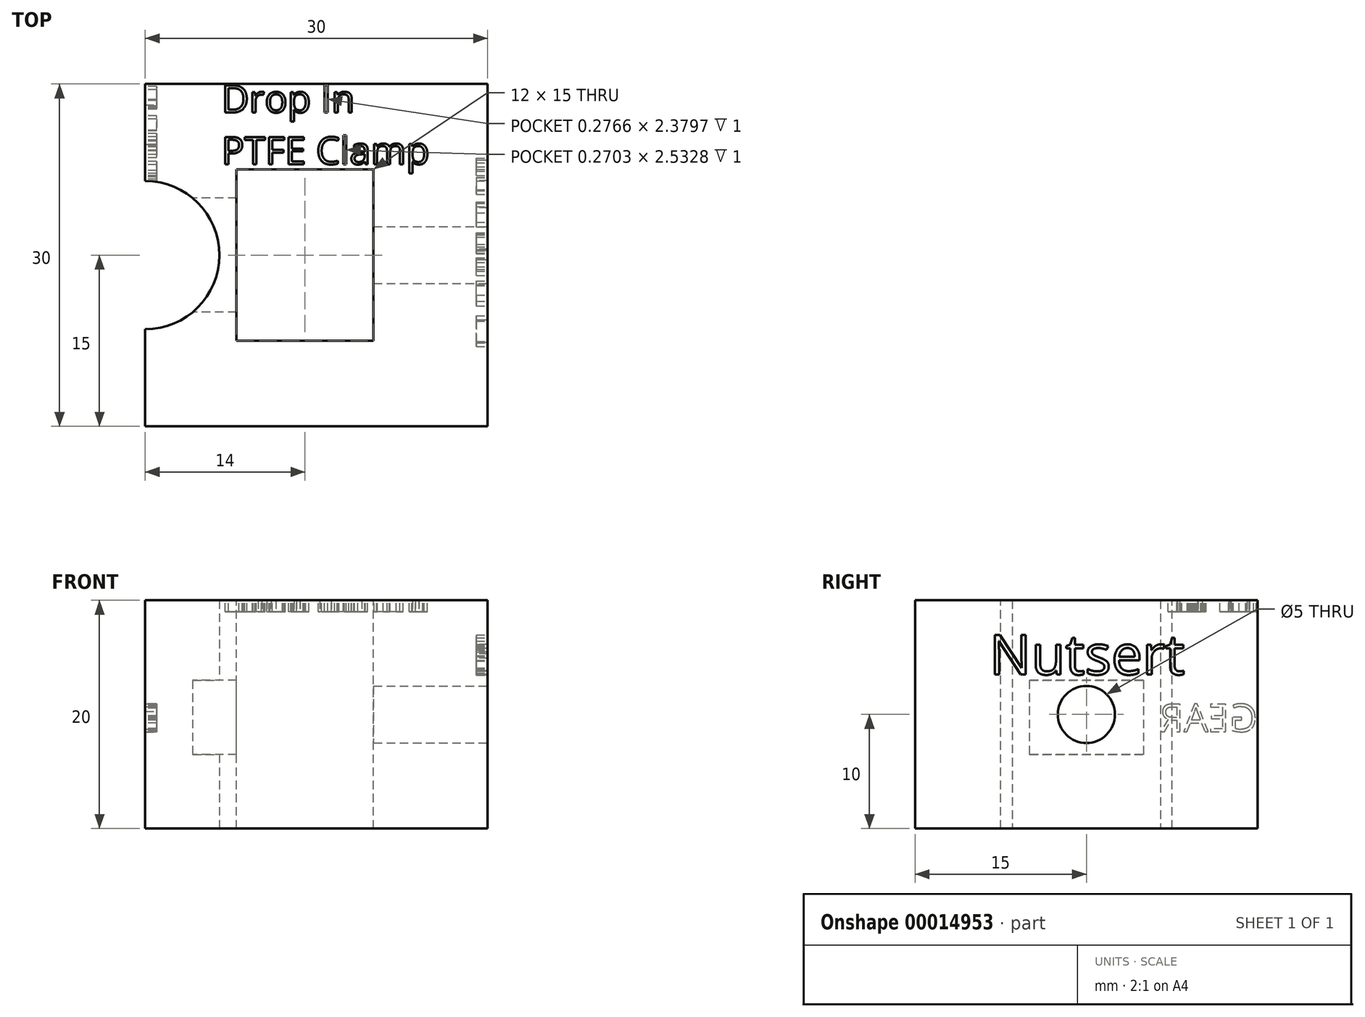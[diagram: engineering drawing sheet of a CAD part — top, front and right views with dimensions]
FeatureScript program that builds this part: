
annotation { "Feature Type Name" : "Feature", "Feature Type Description" : "" }
export const myFeature = defineFeature(function(context is Context, id is Id, definition is map)
    precondition{}
    {
        {
            var Q0;
            Q0=qCreatedBy(makeId("Top.planeOp"),FACE);
            var sketch = newSketch(context, id + "F0", { "sketchPlane" : qUnion([Q0])});
            skLineSegment(sketch, "E0.bottom", {"start": v(-15, 15) * mm, "end": v(15, 15) * mm});
            skLineSegment(sketch, "E0.top", {"start": v(-15, -15) * mm, "end": v(15, -15) * mm});
            skLineSegment(sketch, "E0.right", {"start": v(15, 15) * mm, "end": v(15, -15) * mm});
            skArc(sketch, "E1", {"start": v(-8.5, 0) * mm, "mid": v(-10.4, 4.6) * mm, "end": v(-15, 6.5) * mm});
            skArc(sketch, "E2", {"start": v(-15, -6.5) * mm, "mid": v(-10.4, -4.6) * mm, "end": v(-8.5, 0) * mm});
            skLineSegment(sketch, "E3", {"start": v(-15, 15) * mm, "end": v(-15, 6.5) * mm});
            skLineSegment(sketch, "E4", {"start": v(-15, -15) * mm, "end": v(-15, -6.5) * mm});
            skSolve(sketch);
        }
        {
            var Q0;
            Q0=qSketchRegion(id+"F0",true);
            extrude(context, id + "F1", {"entities" : qUnion([Q0]), "depth" : 20 * mm});
        }
        {
            var Q0;
            Q0=makeQuery(id+"F1.opExtrude","CAP_FACE",FACE,{"disambiguationData":[OSD([sQuery(id+"F0.wireOp",EDGE,"E0.bottom"),sQuery(id+"F0.wireOp",EDGE,"E0.top"),sQuery(id+"F0.wireOp",EDGE,"E0.right"),sQuery(id+"F0.wireOp",EDGE,"E1"),sQuery(id+"F0.wireOp",EDGE,"E2"),sQuery(id+"F0.wireOp",EDGE,"E3"),sQuery(id+"F0.wireOp",EDGE,"E4")])],"isStart":false});
            var sketch = newSketch(context, id + "F2", { "sketchPlane" : qUnion([Q0])});
            skLineSegment(sketch, "E5.bottom", {"start": v(-7, 7.5) * mm, "end": v(5, 7.5) * mm});
            skLineSegment(sketch, "E5.top", {"start": v(-7, -7.5) * mm, "end": v(5, -7.5) * mm});
            skLineSegment(sketch, "E5.left", {"start": v(-7, 7.5) * mm, "end": v(-7, -7.5) * mm});
            skLineSegment(sketch, "E5.right", {"start": v(5, 7.5) * mm, "end": v(5, -7.5) * mm});
            skSolve(sketch);
        }
        {
            var Q0;
            Q0=qSketchRegion(id+"F2",true);
            extrude(context, id + "F3", {"entities" : qUnion([Q0]), "operationType" : NewBodyOperationType.REMOVE, "endBound" : BoundingType.THROUGH_ALL, "oppositeDirection" : true, "depth" : 25 * mm});
        }
        {
            var Q0;
            Q0=makeQuery(id+"F1.opExtrude","SWEPT_FACE",FACE,{"disambiguationData":[OSD([sQuery(id+"F0.wireOp",EDGE,"E0.right")])]});
            var sketch = newSketch(context, id + "F4", { "sketchPlane" : qUnion([Q0])});
            skCircle(sketch, "E6", {"center": v(0, 10) * mm, "radius": 2.5 * mm});
            skSolve(sketch);
        }
        {
            var Q0;
            Q0=qSketchRegion(id+"F4",true);
            var Q1;
            Q1=makeQuery(id+"F3.boolean.opBoolean","COPY",FACE,{"derivedFrom":makeQuery(id+"F3.opExtrude","SWEPT_FACE",FACE,{"disambiguationData":[OSD([sQuery(id+"F2.wireOp",EDGE,"E5.right")])]})});
            extrude(context, id + "F5", {"entities" : qUnion([Q0]), "operationType" : NewBodyOperationType.REMOVE, "endBound" : BoundingType.UP_TO_SURFACE, "oppositeDirection" : true, "endBoundEntityFace" : qUnion([Q1]), "depth" : 25 * mm});
        }
        {
            var Q0;
            Q0=makeQuery(id+"F1.opExtrude","SWEPT_FACE",FACE,{"disambiguationData":[OSD([sQuery(id+"F0.wireOp",EDGE,"E3")])]});
            var sketch = newSketch(context, id + "F6", { "sketchPlane" : qUnion([Q0])});
            skLineSegment(sketch, "E7.bottom", {"start": v(-5, 13) * mm, "end": v(5, 13) * mm});
            skLineSegment(sketch, "E7.top", {"start": v(-5, 6.5) * mm, "end": v(5, 6.5) * mm});
            skLineSegment(sketch, "E7.left", {"start": v(-5, 13) * mm, "end": v(-5, 6.5) * mm});
            skLineSegment(sketch, "E7.right", {"start": v(5, 13) * mm, "end": v(5, 6.5) * mm});
            skSolve(sketch);
        }
        {
            var Q0;
            Q0=qSketchRegion(id+"F6",true);
            var Q1;
            Q1=makeQuery(id+"F3.boolean.opBoolean","COPY",FACE,{"derivedFrom":makeQuery(id+"F3.opExtrude","SWEPT_FACE",FACE,{"disambiguationData":[OSD([sQuery(id+"F2.wireOp",EDGE,"E5.left")])]})});
            extrude(context, id + "F7", {"entities" : qUnion([Q0]), "operationType" : NewBodyOperationType.REMOVE, "endBound" : BoundingType.UP_TO_SURFACE, "oppositeDirection" : true, "endBoundEntityFace" : qUnion([Q1]), "depth" : 25 * mm});
        }
        {
            var Q0;
            Q0=makeQuery(id+"F1.opExtrude","SWEPT_FACE",FACE,{"disambiguationData":[OSD([sQuery(id+"F0.wireOp",EDGE,"E0.right")])]});
            var sketch = newSketch(context, id + "F8", { "sketchPlane" : qUnion([Q0])});
            skText(sketch, "E8", { "text": "Nutsert\n", "fontName": "OpenSans-Regular.ttf"});
            const initialGuessF8  = {"E8": [-0.0085, 0.0135, 1, 0, 0.0035]};
            skSetInitialGuess(sketch, initialGuessF8);
            skSolve(sketch);
        }
        {
            var Q0;
            Q0=qSketchRegion(id+"F8",true);
            extrude(context, id + "F9", {"entities" : qUnion([Q0]), "operationType" : NewBodyOperationType.REMOVE, "oppositeDirection" : true, "depth" : 1 * mm});
        }
        {
            var Q0;
            Q0=makeQuery(id+"F1.opExtrude","SWEPT_FACE",FACE,{"disambiguationData":[OSD([sQuery(id+"F0.wireOp",EDGE,"E3")])]});
            var sketch = newSketch(context, id + "F10", { "sketchPlane" : qUnion([Q0])});
            skText(sketch, "E9", { "text": "GEAR", "fontName": "OpenSans-Regular.ttf"});
            const initialGuessF10  = {"E9": [-0.015, 0.0085, 1, 0, 0.00243]};
            skSetInitialGuess(sketch, initialGuessF10);
            skSolve(sketch);
        }
        {
            var Q0;
            Q0=qSketchRegion(id+"F10",true);
            extrude(context, id + "F11", {"entities" : qUnion([Q0]), "operationType" : NewBodyOperationType.REMOVE, "oppositeDirection" : true, "depth" : 1 * mm});
        }
        {
            var Q0;
            Q0=makeQuery(id+"F1.opExtrude","CAP_FACE",FACE,{"disambiguationData":[OSD([sQuery(id+"F0.wireOp",EDGE,"E0.bottom"),sQuery(id+"F0.wireOp",EDGE,"E0.top"),sQuery(id+"F0.wireOp",EDGE,"E0.right"),sQuery(id+"F0.wireOp",EDGE,"E1"),sQuery(id+"F0.wireOp",EDGE,"E2"),sQuery(id+"F0.wireOp",EDGE,"E3"),sQuery(id+"F0.wireOp",EDGE,"E4")])],"isStart":false});
            var sketch = newSketch(context, id + "F12", { "sketchPlane" : qUnion([Q0])});
            skText(sketch, "E10", { "text": "Drop In \nPTFE Clamp", "fontName": "OpenSans-Regular.ttf"});
            const initialGuessF12  = {"E10": [-0.00833, 0.0125, 1, 0, 0.0024]};
            skSetInitialGuess(sketch, initialGuessF12);
            skSolve(sketch);
        }
        {
            var Q0;
            Q0=qSketchRegion(id+"F12",true);
            extrude(context, id + "F13", {"entities" : qUnion([Q0]), "operationType" : NewBodyOperationType.REMOVE, "oppositeDirection" : true, "depth" : 1 * mm});
        }
    });
